# Revit family: JNRBHSA- 4'
name_source: partatom
category: Mechanical Equipment
revit_build: Autodesk Revit 2017 (Build: 20171027_0315(x64)
units: mm (PartAtom-declared; Revit-internal decimal feet)

## family parameters
Always vertical = Yes
Cut with Voids When Loaded = No
OmniClass Number = 23.40.40.11.17
OmniClass Title = Refrigerated Cases
Part Type = Normal
Room Calculation Point = No
Round Connector Dimension = Use Radius
Shared = No
Work Plane-Based = Yes

## types (2) — shared parameters
22" Shelf = Yes
24hr Energy Usage (kWh) = 20.1 (kWh)
Certifications = NSF 7, UL471, CSA
Condensing  Data Volts = 208 V
Condensing Data  Phase = 1
Condensing Frequency (Hz) = 60 (Hz)
DATE = 02/09/2016
DISCHARGE AIR TEMP. = 33 °F
DISCHARGE AIR VELOCITY = 230 FPM
Default Elevation = 48"
Defrost Num Day = 2
Defrost Termination = 40 °F
Defrost Type = TIMED-OFF DEFROST
Defrosts Per Day_2 = 2
Description = Narrow Reach-In Self-Contained Merchandiser
Discharge Air (°F) = 33°F
Discharge Air Velocity (FPM) = 230 (FPM)
Doors/Length = 5
EQUIPMENT DESCRIPTION = Narrow Reach-In Self-Contained Merchandiser
EQUIPMENT MARK = JNRBHSA
GLASS = Glass
Height = 82 1/2"
Horsepower = 1/2
Item Description = Narrow Reach-In Self-Contained Merchandiser
Lbs. of Refrigerant = 3.5
Legend Number = JNRBHSA-PV
Locked Rotor (LRA) Amps = 34 A
Manufacturer = HILL PHOENIX
Model = JNRBHSA-PV
NUMBER OF DOORS = 5
PAINTED METAL UPPER SHELF = PAINTED SHELVES
Provided Overcurrent Protection = 20
Refrig Charge Lbs = 0
Refrigerant = R404A
Running Load (RLA) Amps = 9 A
Superheat Set Point @ Bulb (°F) = 6-8°
System Data Frequency (Hz) = 60 (Hz)
System Data Phase = 1
System Data Volts = 208 V
Timed-Off Defrost Fail-Safe (Min) = 60 (Min)
Timed-Off Defrost Termination Temp_2 = 40°F
URL = http://www.hillphoenix.com
Width = 34 7/8"
zero-valued in all types: Evap Temp, Load Mbh

## per-type parameters (varying)
| type | CENTER LINE & DRAIN | CONDENSING UNIT LOCATION | Condenser | DOOR CONFIGURATION | Length |
| 2 Door | 30" | 54" | 15" | MASTER DOOR : 30" X 68 3/8" 2 DOOR A SWING (LEFT OPENING) | 60" |
| 4' | 24" | 40" | 9" | MASTER DOOR : 24" x 68 3/8" 2 DOOR FRENCH SWING | 48" |

## geometry (parser evidence)
native form markers: Blend x12, Sweep x5
no freeform markers — native parametric forms only
